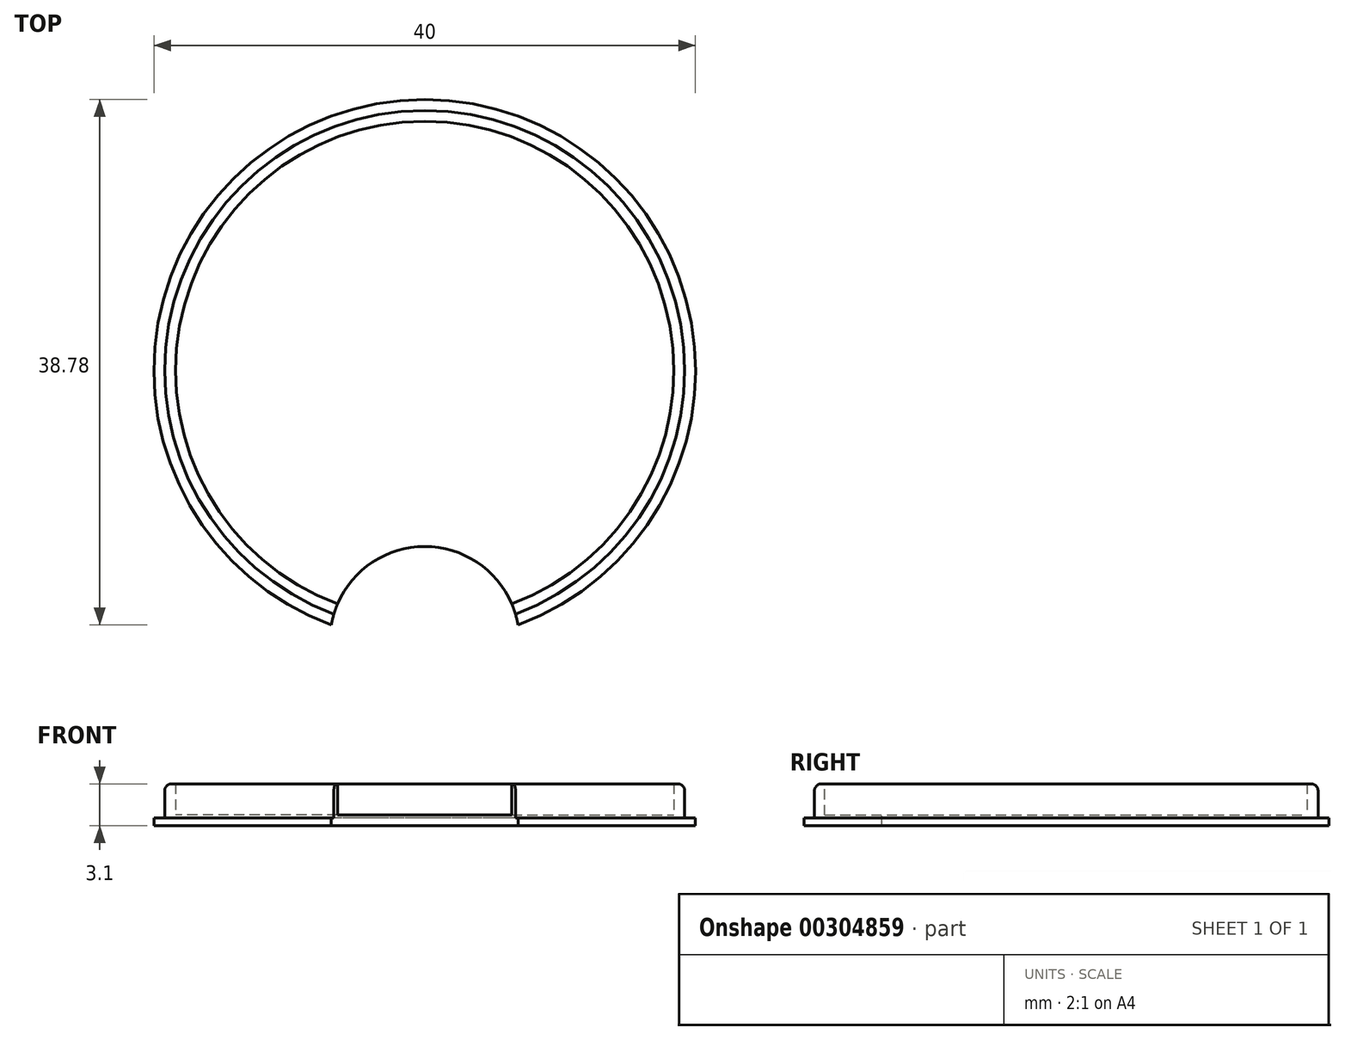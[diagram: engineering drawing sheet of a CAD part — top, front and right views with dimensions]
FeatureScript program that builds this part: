
annotation { "Feature Type Name" : "Feature", "Feature Type Description" : "" }
export const myFeature = defineFeature(function(context is Context, id is Id, definition is map)
    precondition{}
    {
        {
            var Q0;
            Q0=qCreatedBy(makeId("Top.planeOp"),FACE);
            var sketch = newSketch(context, id + "F0", { "sketchPlane" : qUnion([Q0])});
            skCircle(sketch, "E0", {"center": v(0, 0) * mm, "radius": 20 * mm});
            skSolve(sketch);
        }
        {
            var Q0;
            Q0=makeQuery(id+"F0.imprint","IMPRINT",FACE,{"disambiguationData":[TD([[makeQuery(id+"F0.imprint","IMPRINT",EDGE,{"derivedFrom":sQuery(id+"F0.wireOp",EDGE,"E0")}),1.0]])]});
            extrude(context, id + "F1", {"entities" : qUnion([Q0]), "depth" : 0.6 * mm});
        }
        {
            var Q0;
            Q0=qCreatedBy(makeId("Top.planeOp"),FACE);
            cPlane(context, id + "F2", {"entities" : qUnion([Q0]), "cplaneType" : CPlaneType.OFFSET, "offset" : 0.6 * mm, "width" : 150 * mm, "height" : 150 * mm});
        }
        {
            var Q0;
            Q0=makeQuery(id+"F1.opExtrude","CAP_FACE",FACE,{"disambiguationData":[OSD([sQuery(id+"F0.wireOp",EDGE,"E0")])],"isStart":false});
            var sketch = newSketch(context, id + "F3", { "sketchPlane" : qUnion([Q0])});
            skCircle(sketch, "E1", {"center": v(0, 0) * mm, "radius": 19.2 * mm});
            skSolve(sketch);
        }
        {
            var Q0;
            Q0=makeQuery(id+"F3.imprint","IMPRINT",FACE,{"disambiguationData":[TD([[makeQuery(id+"F3.imprint","IMPRINT",EDGE,{"derivedFrom":sQuery(id+"F3.wireOp",EDGE,"E1")}),1.0]])]});
            extrude(context, id + "F4", {"entities" : qUnion([Q0]), "operationType" : NewBodyOperationType.ADD, "depth" : 2.5 * mm});
        }
        {
            var Q0;
            Q0=makeQuery(id+"F4.opExtrude","CAP_FACE",FACE,{"disambiguationData":[OSD([sQuery(id+"F3.wireOp",EDGE,"E1")])],"isStart":false});
            shell(context, id + "F5", {"entities" : qUnion([Q0]), "thickness" : 0.8 * mm});
        }
        {
            var Q0;
            Q0=makeQuery(id+"F4.opExtrude","CAP_EDGE",EDGE,{"disambiguationData":[OSD([sQuery(id+"F3.wireOp",EDGE,"E1")])],"isStart":false});
            fillet(context, id + "F6", {"entities" : qUnion([Q0]), "radius" : 0.5 * mm, "tangentPropagation" : true, "allowEdgeOverflow" : false});
        }
        {
            var Q0;
            Q0=qCreatedBy(id+"F2.planeOp",FACE);
            cPlane(context, id + "F7", {"entities" : qUnion([Q0]), "cplaneType" : CPlaneType.OFFSET, "offset" : 2.5 * mm, "width" : 150 * mm, "height" : 150 * mm});
        }
        {
            var Q0;
            Q0=qCreatedBy(id+"F7.planeOp",FACE);
            var sketch = newSketch(context, id + "F8", { "sketchPlane" : qUnion([Q0])});
            skCircle(sketch, "E2.0", {"center": v(0, 0) * mm, "radius": 20 * mm});
            skCircle(sketch, "E3", {"center": v(0, -20) * mm, "radius": 7 * mm});
            skSolve(sketch);
        }
        {
            var Q0;
            Q0=sQuery(id+"F8.wireOp",VERTEX,"E3.center");
            var Q1;
            Q1=makeQuery(id+"F1.opExtrude","SWEPT_BODY",BODY,{"disambiguationData":[OSD([sQuery(id+"F0.wireOp",EDGE,"E0")])]});
            hole(context, id + "F9", {"style" : HoleStyle.SIMPLE, "endStyle" : HoleEndStyle.BLIND, "holeDiameter" : 14 * mm, "holeDepth" : 4 * mm, "tappedDepth" : 12 * mm, "tapClearance" : 3, "locations" : qUnion([Q0]), "scope" : qUnion([Q1])});
        }
    });
